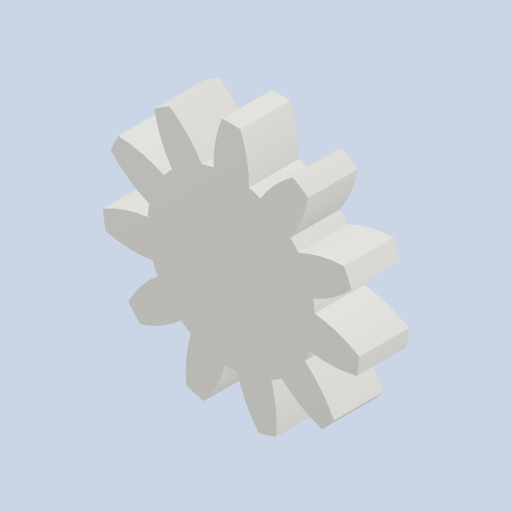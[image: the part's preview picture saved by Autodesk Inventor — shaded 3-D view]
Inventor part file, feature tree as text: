
AUTODESK INVENTOR PART (.ipt)
format: ipt  version: 2022 (Build 260153000, 153)  size: 186,368 bytes
history: native  units: mm (DEFAULTED — no unit token found)
features: plane x3, other x3, sketch x2, extrude x1
ambient origin geometry x8: Origin, YZ Plane, XZ Plane, XY Plane, X Axis, Y Axis, Z Axis, Center Point
bodies: Solid1 (feature_tree)
feature tree (9):
  extrude  "Extrusion1"  Depth=5.0mm TaperAngle=0.0deg
  plane  "Work Plane2"
  plane  "Work Plane8"
  plane  "Work Plane9"
  other  "Цилиндрическое зубчатое зацепление"
  sketch  "Sketch1"  dims[d0=25.891697mm d1=5.0mm d2=0.0mm]
  sketch  "Sketch2"  dims[d3=22.0mm d4=10.0mm d5=0.0mm d16=40.945848mm d17=0.0mm d34=2.855993mm d39=0.0mm d41=0.0mm d43=40.945848mm d46=40.945848mm d47=0.0mm d48=0.0mm]
  other  "Srf1"
  other  "Средний диаметр"
